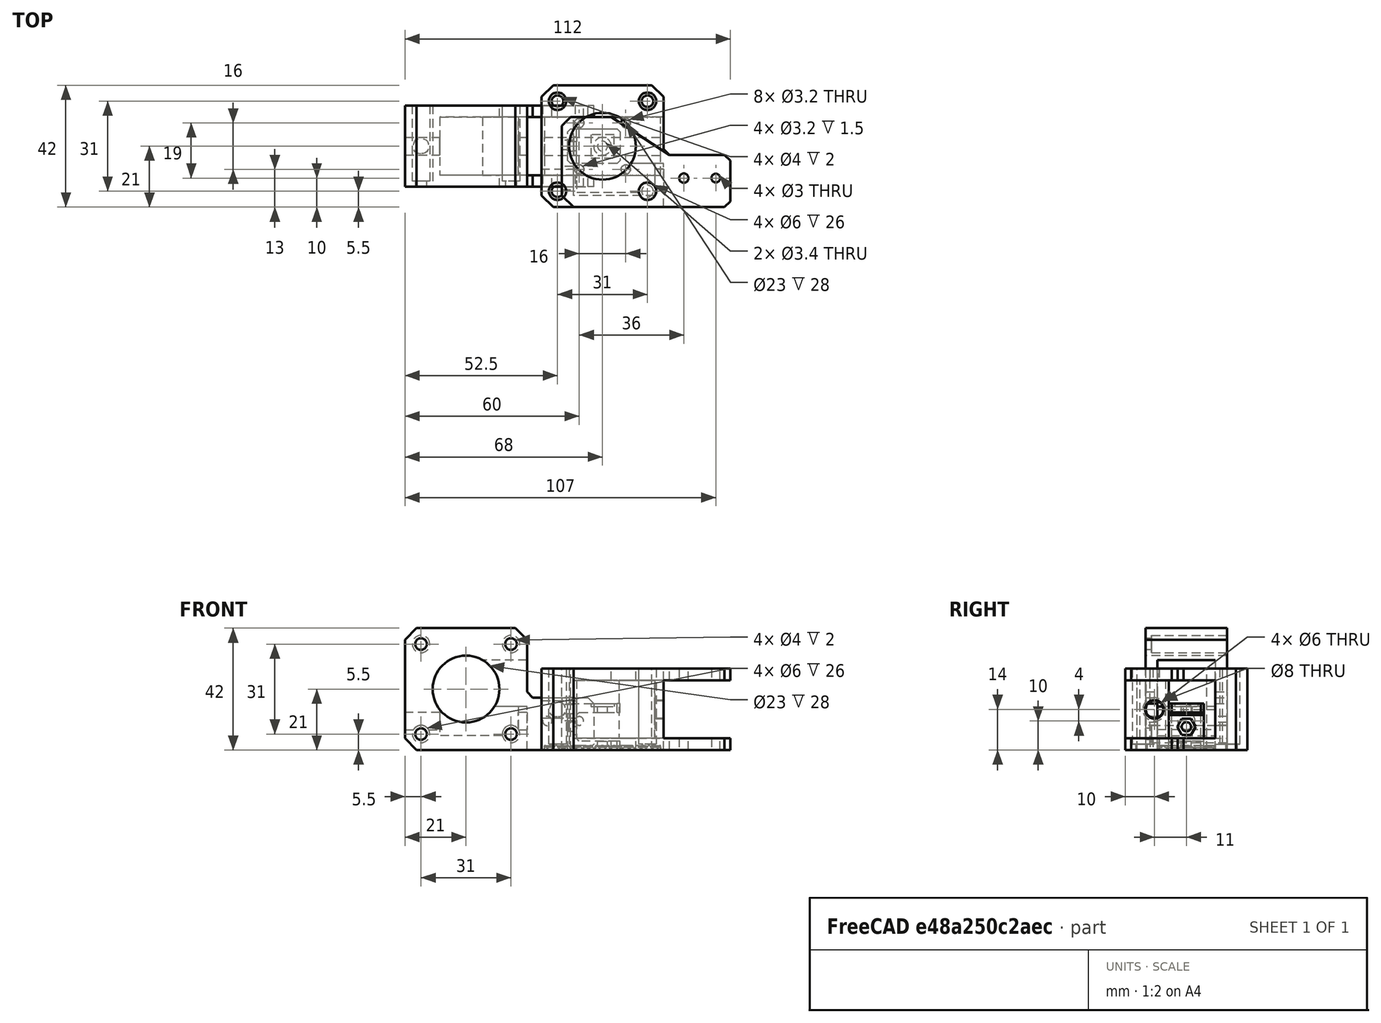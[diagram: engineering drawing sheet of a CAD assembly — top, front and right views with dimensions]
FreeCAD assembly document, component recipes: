
FREECAD ASSEMBLY — COMPONENT RECIPES ("LinearRailMod")

This assembly document has 5 components, labeled P0..P4 below (a component is one placed body or linked part). 5 of them carry a construction recipe — the FreeCAD feature program that regenerates the part from scratch, quoted from this document or its linked companion documents; the rest are supplied as boundary geometry only. No exploded tour is included for this assembly.
COMPONENT P0 — recipe-attached ("Motor", modeled in this document).
Construction recipe (the document's own serialized feature program — sketch geometry with constraints, then the solid features built on it; lengths are millimeters unless a unit is written):

FEATURE [Sketcher::SketchObject] Sketch
  ArcFitTolerance = 1e-06
  AttachmentSupport = -> [XY_Plane001]
  FullyConstrained = false
  MakeInternals = false
  MapMode = 5
  sketch-geometry (20):
    g0: GeomPoint [constr] X=0 Y=0 Z=0
    g1: LineSegment StartX=-17 StartY=21 StartZ=0 EndX=-21 EndY=17 EndZ=0
    g2: LineSegment StartX=-21 StartY=-17 StartZ=0 EndX=-17 EndY=-21 EndZ=0
    g3: LineSegment StartX=17 StartY=21 StartZ=0 EndX=21 EndY=17 EndZ=0
    g4: Circle CenterX=-15.5 CenterY=-15.5 CenterZ=0 NormalX=0 NormalY=0 NormalZ=1 AngleXU=0 Radius=2
    g5: Circle CenterX=15.5 CenterY=-15.5 CenterZ=0 NormalX=0 NormalY=0 NormalZ=1 AngleXU=0 Radius=2
    g6: Circle CenterX=15.5 CenterY=15.5 CenterZ=0 NormalX=0 NormalY=0 NormalZ=1 AngleXU=0 Radius=2
    g7: LineSegment StartX=-21 StartY=17 StartZ=0 EndX=-21 EndY=-17 EndZ=0
    g8: LineSegment StartX=-17 StartY=-21 StartZ=0 EndX=42 EndY=-21 EndZ=0
    g9: LineSegment StartX=-17 StartY=21 StartZ=0 EndX=17 EndY=21 EndZ=0
    g10: LineSegment StartX=21 StartY=17 StartZ=0 EndX=21 EndY=-1 EndZ=0
    g11: LineSegment StartX=44 StartY=-19 StartZ=0 EndX=42 EndY=-21 EndZ=0
    g12: Circle CenterX=-15.5 CenterY=15.5 CenterZ=0 NormalX=0 NormalY=0 NormalZ=1 AngleXU=0 Radius=2
    g13: Circle CenterX=0 CenterY=0 CenterZ=0 NormalX=0 NormalY=0 NormalZ=1 AngleXU=0 Radius=11.5
    g14: Circle CenterX=28 CenterY=-11 CenterZ=0 NormalX=0 NormalY=0 NormalZ=1 AngleXU=0 Radius=1.6
    g15: LineSegment StartX=21 StartY=-1 StartZ=0 EndX=23 EndY=-3 EndZ=0
    g16: LineSegment StartX=23 StartY=-3 StartZ=0 EndX=42 EndY=-3 EndZ=0
    g17: LineSegment StartX=42 StartY=-3 StartZ=0 EndX=44 EndY=-5 EndZ=0
    g18: LineSegment StartX=44 StartY=-5 StartZ=0 EndX=44 EndY=-19 EndZ=0
    g19: Circle CenterX=39 CenterY=-11 CenterZ=0 NormalX=0 NormalY=0 NormalZ=1 AngleXU=0 Radius=1.5
  constraints (19):
    c: Coincident(g7,g1)
    c: Coincident(g7,g2)
    c: Vertical(g7)
    c: Coincident(g8,g2)
    c: Horizontal(g8)
    c: Coincident(g9,g1)
    c: Coincident(g9,g3)
    c: Horizontal(g9)
    c: Coincident(g10,g3)
    c: Vertical(g10)
    c: Coincident(g11,g8)
    c: Coincident(g13,g0)
    c: Coincident(g15,g10)
    c: Coincident(g16,g15)
    c: Horizontal(g16)
    c: Coincident(g17,g16)
    c: Coincident(g18,g17)
    c: Coincident(g18,g11)
    c: Vertical(g18)
FEATURE [PartDesign::Pad] Pad
  Direction = (0,0,1)
  Length = 28
  Length2 = 10
  Profile = -> Sketch
  ReferenceAxis = -> Sketch [N_Axis]
  Refine = true
  Suppressed = false
  Type = 0
FEATURE [Sketcher::SketchObject] Sketch003
  ArcFitTolerance = 1e-06
  AttachmentSupport = -> [Pad]
  FullyConstrained = false
  MakeInternals = false
  MapMode = 5
  Placement = pos=(0,-21,0) rot=(1,0,0;1.5708rad)
  sketch-geometry (4):
    g0: LineSegment StartX=21 StartY=24 StartZ=0 EndX=21 EndY=4 EndZ=0
    g1: LineSegment StartX=21 StartY=4 StartZ=0 EndX=50 EndY=4 EndZ=0
    g2: LineSegment StartX=50 StartY=4 StartZ=0 EndX=50 EndY=24 EndZ=0
    g3: LineSegment StartX=50 StartY=24 StartZ=0 EndX=21 EndY=24 EndZ=0
  constraints (8):
    c: Coincident(g0,g1)
    c: Coincident(g1,g2)
    c: Coincident(g2,g3)
    c: Coincident(g3,g0)
    c: Vertical(g0)
    c: Vertical(g2)
    c: Horizontal(g1)
    c: Horizontal(g3)
FEATURE [PartDesign::Pocket] Pocket
  BaseFeature = -> Pad
  Direction = (0,1,-2e-16)
  Length = 42
  Length2 = 5
  Profile = -> Sketch003
  ReferenceAxis = -> Sketch003 [N_Axis]
  Refine = true
  Suppressed = false
  Type = 0
FEATURE [Sketcher::SketchObject] Sketch004
  ArcFitTolerance = 1e-06
  AttachmentSupport = -> [Pocket]
  FullyConstrained = false
  MakeInternals = false
  MapMode = 5
  Placement = pos=(0,0,28) rot=(0,0,1;0rad)
  sketch-geometry (4):
    g0: Circle CenterX=-15.5 CenterY=-15.5 CenterZ=0 NormalX=0 NormalY=0 NormalZ=1 AngleXU=0 Radius=3
    g1: Circle CenterX=-15.5 CenterY=15.5 CenterZ=0 NormalX=0 NormalY=0 NormalZ=1 AngleXU=0 Radius=3
    g2: Circle CenterX=15.5 CenterY=15.5 CenterZ=0 NormalX=0 NormalY=0 NormalZ=1 AngleXU=0 Radius=3
    g3: Circle CenterX=15.5 CenterY=-15.5 CenterZ=0 NormalX=0 NormalY=0 NormalZ=1 AngleXU=0 Radius=3
FEATURE [PartDesign::Pocket] Pocket001
  BaseFeature = -> Pocket
  Direction = (0,0,-1)
  Length = 26
  Length2 = 5
  Profile = -> Sketch004
  ReferenceAxis = -> Sketch004 [N_Axis]
  Refine = true
  Suppressed = false
  Type = 0
FEATURE [Sketcher::SketchObject] Sketch005
  ArcFitTolerance = 1e-06
  AttachmentSupport = -> [Pocket001]
  FullyConstrained = false
  MakeInternals = false
  MapMode = 5
  Placement = pos=(21,0,0) rot=(0.57735,0.57735,0.57735;2.0944rad)
  sketch-geometry (1):
    g0: Circle CenterX=-11 CenterY=14 CenterZ=0 NormalX=0 NormalY=0 NormalZ=1 AngleXU=0 Radius=3
FEATURE [PartDesign::Pocket] Pocket002
  BaseFeature = -> Pocket001
  Direction = (-1,0,0)
  Length = 42
  Length2 = 5
  Profile = -> Sketch005
  ReferenceAxis = -> Sketch005 [N_Axis]
  Refine = true
  Suppressed = false
  Type = 0
FEATURE [Sketcher::SketchObject] Sketch006
  ArcFitTolerance = 1e-06
  AttachmentSupport = -> [Pocket002]
  FullyConstrained = false
  MakeInternals = false
  MapMode = 5
  Placement = pos=(21,0,0) rot=(0.57735,0.57735,0.57735;2.0944rad)
  sketch-geometry (4):
    g0: LineSegment StartX=-6 StartY=24 StartZ=0 EndX=-6 EndY=4 EndZ=0
    g1: LineSegment StartX=-6 StartY=4 StartZ=0 EndX=10 EndY=4 EndZ=0
    g2: LineSegment StartX=10 StartY=4 StartZ=0 EndX=10 EndY=24 EndZ=0
    g3: LineSegment StartX=10 StartY=24 StartZ=0 EndX=-6 EndY=24 EndZ=0
  constraints (8):
    c: Coincident(g0,g1)
    c: Coincident(g1,g2)
    c: Coincident(g2,g3)
    c: Coincident(g3,g0)
    c: Vertical(g0)
    c: Vertical(g2)
    c: Horizontal(g1)
    c: Horizontal(g3)
FEATURE [PartDesign::Pocket] Pocket003
  BaseFeature = -> Pocket002
  Direction = (-1,0,0)
  Length = 16
  Length2 = 5
  Profile = -> Sketch006
  ReferenceAxis = -> Sketch006 [N_Axis]
  Refine = true
  Suppressed = false
  Type = 0
FEATURE [Sketcher::SketchObject] Sketch007
  ArcFitTolerance = 1e-06
  AttachmentSupport = -> [Pocket003]
  FullyConstrained = false
  MakeInternals = false
  MapMode = 5
  Placement = pos=(0,-6,0) rot=(0,0.707107,0.707107;3.14159rad)
  sketch-geometry (4):
    g0: LineSegment StartX=-18 StartY=24.038 StartZ=0 EndX=-18 EndY=4.03804 EndZ=0
    g1: LineSegment StartX=-18 StartY=4.03804 StartZ=0 EndX=9 EndY=4.03804 EndZ=0
    g2: LineSegment StartX=9 StartY=4.03804 StartZ=0 EndX=9 EndY=24.038 EndZ=0
    g3: LineSegment StartX=9 StartY=24.038 StartZ=0 EndX=-18 EndY=24.038 EndZ=0
  constraints (8):
    c: Coincident(g0,g1)
    c: Coincident(g1,g2)
    c: Coincident(g2,g3)
    c: Coincident(g3,g0)
    c: Vertical(g0)
    c: Vertical(g2)
    c: Horizontal(g1)
    c: Horizontal(g3)
FEATURE [PartDesign::Pocket] Pocket004
  BaseFeature = -> Pocket003
  Direction = (0,-1,2e-16)
  Length = 10
  Length2 = 5
  Profile = -> Sketch007
  ReferenceAxis = -> Sketch007 [N_Axis]
  Refine = true
  Suppressed = false
  Type = 0
FEATURE [PartDesign::Body] Body
  AllowCompound = false
  Group = -> [Sketch,Pad,Sketch003,Pocket,Sketch004,Pocket001,Sketch005,Pocket002,Sketch006,Pocket003,Sketch007,Pocket004]
  Origin = -> Origin001
  Tip = -> Pocket004
COMPONENT P1 — recipe-attached ("IdlerGearFrame", modeled in this document).
Construction recipe (the document's own serialized feature program — sketch geometry with constraints, then the solid features built on it; lengths are millimeters unless a unit is written):

FEATURE [Sketcher::SketchObject] Sketch008
  ArcFitTolerance = 1e-06
  AttachmentSupport = -> [XY_Plane007]
  FullyConstrained = false
  MakeInternals = false
  MapMode = 5
  sketch-geometry (12):
    g0: LineSegment StartX=-14 StartY=-17 StartZ=0 EndX=-10 EndY=-21 EndZ=0
    g1: LineSegment StartX=-14 StartY=7 StartZ=0 EndX=-14 EndY=-17 EndZ=0
    g2: LineSegment StartX=-10 StartY=-21 StartZ=0 EndX=42 EndY=-21 EndZ=0
    g3: LineSegment StartX=44 StartY=-19 StartZ=0 EndX=42 EndY=-21 EndZ=0
    g4: Circle CenterX=28 CenterY=-11 CenterZ=0 NormalX=0 NormalY=0 NormalZ=1 AngleXU=0 Radius=1.6
    g5: LineSegment StartX=23 StartY=-3 StartZ=0 EndX=42 EndY=-3 EndZ=0
    g6: LineSegment StartX=42 StartY=-3 StartZ=0 EndX=44 EndY=-5 EndZ=0
    g7: LineSegment StartX=44 StartY=-5 StartZ=0 EndX=44 EndY=-19 EndZ=0
    g8: Circle CenterX=39 CenterY=-11 CenterZ=0 NormalX=0 NormalY=0 NormalZ=1 AngleXU=0 Radius=1.5
    g9: LineSegment StartX=23 StartY=-3 StartZ=0 EndX=3 EndY=10 EndZ=0
    g10: LineSegment StartX=3 StartY=10 StartZ=0 EndX=-11 EndY=10 EndZ=0
    g11: LineSegment StartX=-11 StartY=10 StartZ=0 EndX=-14 EndY=7 EndZ=0
  constraints (15):
    c: Coincident(g1,g0)
    c: Vertical(g1)
    c: Coincident(g2,g0)
    c: Horizontal(g2)
    c: Coincident(g3,g2)
    c: Horizontal(g5)
    c: Coincident(g6,g5)
    c: Coincident(g7,g6)
    c: Coincident(g7,g3)
    c: Vertical(g7)
    c: Coincident(g5,g9)
    c: Coincident(g9,g10)
    c: Horizontal(g10)
    c: Coincident(g10,g11)
    c: Coincident(g11,g1)
FEATURE [PartDesign::Pad] Pad002
  Direction = (0,0,1)
  Length = 28
  Length2 = 10
  Profile = -> Sketch008
  ReferenceAxis = -> Sketch008 [N_Axis]
  Refine = true
  Suppressed = false
  Type = 0
FEATURE [Sketcher::SketchObject] Sketch018
  ArcFitTolerance = 1e-06
  AttachmentSupport = -> [Pad002]
  FullyConstrained = false
  MakeInternals = false
  MapMode = 5
  Placement = pos=(0,-21,0) rot=(1,0,0;1.5708rad)
  sketch-geometry (4):
    g0: LineSegment StartX=21 StartY=24 StartZ=0 EndX=21 EndY=4 EndZ=0
    g1: LineSegment StartX=21 StartY=4 StartZ=0 EndX=50 EndY=4 EndZ=0
    g2: LineSegment StartX=50 StartY=4 StartZ=0 EndX=50 EndY=24 EndZ=0
    g3: LineSegment StartX=50 StartY=24 StartZ=0 EndX=21 EndY=24 EndZ=0
  constraints (8):
    c: Coincident(g0,g1)
    c: Coincident(g1,g2)
    c: Coincident(g2,g3)
    c: Coincident(g3,g0)
    c: Vertical(g0)
    c: Vertical(g2)
    c: Horizontal(g1)
    c: Horizontal(g3)
FEATURE [PartDesign::Pocket] Pocket011
  BaseFeature = -> Pad002
  Direction = (0,1,-2e-16)
  Length = 42
  Length2 = 5
  Profile = -> Sketch018
  ReferenceAxis = -> Sketch018 [N_Axis]
  Refine = true
  Suppressed = false
  Type = 0
FEATURE [Sketcher::SketchObject] Sketch020
  ArcFitTolerance = 1e-06
  FullyConstrained = false
  MakeInternals = false
  MapMode = 5
  Placement = pos=(21,0,0) rot=(0.57735,0.57735,0.57735;2.0944rad)
  sketch-geometry (4):
    g0: LineSegment StartX=-6 StartY=24 StartZ=0 EndX=-6 EndY=4 EndZ=0
    g1: LineSegment StartX=-6 StartY=4 StartZ=0 EndX=17 EndY=4 EndZ=0
    g2: LineSegment StartX=17 StartY=4 StartZ=0 EndX=17 EndY=24 EndZ=0
    g3: LineSegment StartX=17 StartY=24 StartZ=0 EndX=-6 EndY=24 EndZ=0
  constraints (8):
    c: Coincident(g0,g1)
    c: Coincident(g1,g2)
    c: Coincident(g2,g3)
    c: Coincident(g3,g0)
    c: Vertical(g0)
    c: Vertical(g2)
    c: Horizontal(g1)
    c: Horizontal(g3)
FEATURE [PartDesign::Pocket] Pocket013
  BaseFeature = -> Pocket011
  Direction = (-1,0,0)
  Length = 31
  Length2 = 5
  Profile = -> Sketch020
  ReferenceAxis = -> Sketch020 [N_Axis]
  Refine = true
  Suppressed = false
  Type = 0
FEATURE [Sketcher::SketchObject] Sketch021
  ArcFitTolerance = 1e-06
  AttachmentSupport = -> [Pocket013]
  FullyConstrained = false
  MakeInternals = false
  MapMode = 5
  Placement = pos=(0,-6,0) rot=(0,0.707107,0.707107;3.14159rad)
  sketch-geometry (4):
    g0: LineSegment StartX=10 StartY=24 StartZ=0 EndX=-18 EndY=24 EndZ=0
    g1: LineSegment StartX=-18 StartY=24 StartZ=0 EndX=-18 EndY=4 EndZ=0
    g2: LineSegment StartX=-18 StartY=4 StartZ=0 EndX=10 EndY=4 EndZ=0
    g3: LineSegment StartX=10 StartY=4 StartZ=0 EndX=10 EndY=24 EndZ=0
  constraints (8):
    c: Coincident(g0,g1)
    c: Coincident(g1,g2)
    c: Coincident(g2,g3)
    c: Coincident(g3,g0)
    c: Horizontal(g0)
    c: Horizontal(g2)
    c: Vertical(g1)
    c: Vertical(g3)
FEATURE [PartDesign::Pocket] Pocket014
  BaseFeature = -> Pocket013
  Direction = (0,-1,2e-16)
  Length = 11
  Length2 = 5
  Profile = -> Sketch021
  ReferenceAxis = -> Sketch021 [N_Axis]
  Refine = true
  Suppressed = false
  Type = 0
FEATURE [Sketcher::SketchObject] Sketch022
  ArcFitTolerance = 1e-06
  AttachmentSupport = -> [Pocket014]
  FullyConstrained = false
  MakeInternals = false
  MapMode = 5
  Placement = pos=(21,0,0) rot=(0.57735,0.57735,0.57735;2.0944rad)
  sketch-geometry (1):
    g0: Circle CenterX=-11 CenterY=14 CenterZ=0 NormalX=0 NormalY=0 NormalZ=1 AngleXU=0 Radius=3.2
FEATURE [PartDesign::Pocket] Pocket015
  BaseFeature = -> Pocket014
  Direction = (-1,0,0)
  Length = 5
  Length2 = 5
  Profile = -> Sketch022
  ReferenceAxis = -> Sketch022 [N_Axis]
  Refine = true
  Suppressed = false
  Type = 0
FEATURE [Sketcher::SketchObject] Sketch023
  ArcFitTolerance = 1e-06
  AttachmentSupport = -> [Pocket015]
  FullyConstrained = false
  MakeInternals = false
  MapMode = 5
  Placement = pos=(-14,0,0) rot=(0.57735,-0.57735,-0.57735;2.0944rad)
  sketch-geometry (2):
    g0: Circle CenterX=11 CenterY=14 CenterZ=0 NormalX=0 NormalY=0 NormalZ=1 AngleXU=0 Radius=4
    g1: Circle CenterX=-0.5 CenterY=14 CenterZ=0 NormalX=0 NormalY=0 NormalZ=1 AngleXU=0 Radius=1.6
FEATURE [PartDesign::Pocket] Pocket016
  BaseFeature = -> Pocket015
  Direction = (1,0,0)
  Length = 5
  Length2 = 5
  Profile = -> Sketch023
  ReferenceAxis = -> Sketch023 [N_Axis]
  Refine = true
  Suppressed = false
  Type = 0
FEATURE [PartDesign::Body] Body002
  AllowCompound = false
  Group = -> [Sketch008,Pad002,Sketch018,Pocket011,Sketch020,Pocket013,Sketch021,Pocket014,Sketch022,Pocket015,Sketch023,Pocket016]
  Origin = -> Origin007
  Tip = -> Pocket016
COMPONENT P2 — recipe-attached ("IdlerGear", modeled in this document).
Construction recipe (the document's own serialized feature program — sketch geometry with constraints, then the solid features built on it; lengths are millimeters unless a unit is written):

FEATURE [Sketcher::SketchObject] Sketch009
  ArcFitTolerance = 1e-06
  AttachmentSupport = -> [XY_Plane006]
  FullyConstrained = false
  MakeInternals = false
  MapMode = 5
  sketch-geometry (10):
    g0: Circle [constr] CenterX=0 CenterY=0 CenterZ=0 NormalX=0 NormalY=0 NormalZ=1 AngleXU=0 Radius=6.5
    g1: LineSegment StartX=-12 StartY=5 StartZ=0 EndX=-11 EndY=6 EndZ=0
    g2: LineSegment StartX=-11 StartY=6 StartZ=0 EndX=5 EndY=6 EndZ=0
    g3: LineSegment StartX=5 StartY=6 StartZ=0 EndX=6 EndY=5 EndZ=0
    g4: LineSegment StartX=6 StartY=5 StartZ=0 EndX=6 EndY=-5 EndZ=0
    g5: LineSegment StartX=6 StartY=-5 StartZ=0 EndX=5 EndY=-6 EndZ=0
    g6: LineSegment StartX=5 StartY=-6 StartZ=0 EndX=-11 EndY=-6 EndZ=0
    g7: LineSegment StartX=-11 StartY=-6 StartZ=0 EndX=-12 EndY=-5 EndZ=0
    g8: LineSegment StartX=-12 StartY=-5 StartZ=0 EndX=-12 EndY=5 EndZ=0
    g9: Circle CenterX=0 CenterY=0 CenterZ=0 NormalX=0 NormalY=0 NormalZ=1 AngleXU=0 Radius=1.6
  constraints (12):
    c: Coincident(g1,g2)
    c: Horizontal(g2)
    c: Coincident(g2,g3)
    c: Coincident(g3,g4)
    c: Vertical(g4)
    c: Coincident(g4,g5)
    c: Coincident(g5,g6)
    c: Horizontal(g6)
    c: Coincident(g6,g7)
    c: Coincident(g7,g8)
    c: Coincident(g8,g1)
    c: Vertical(g8)
FEATURE [PartDesign::Pad] Pad001
  Direction = (0,0,1)
  Length = 16
  Length2 = 10
  Profile = -> Sketch009
  ReferenceAxis = -> Sketch009 [N_Axis]
  Refine = true
  Suppressed = false
  Type = 0
FEATURE [Sketcher::SketchObject] Sketch013
  ArcFitTolerance = 1e-06
  FullyConstrained = false
  MakeInternals = false
  MapMode = 5
  Placement = pos=(0,-6,0) rot=(1,0,0;1.5708rad)
  sketch-geometry (6):
    g0: LineSegment StartX=-9 StartY=12 StartZ=0 EndX=-8 EndY=13 EndZ=0
    g1: LineSegment StartX=-8 StartY=13 StartZ=0 EndX=5 EndY=13 EndZ=0
    g2: LineSegment StartX=5 StartY=13 StartZ=0 EndX=5 EndY=3 EndZ=0
    g3: LineSegment StartX=5 StartY=3 StartZ=0 EndX=-8 EndY=3 EndZ=0
    g4: LineSegment StartX=-8 StartY=3 StartZ=0 EndX=-9 EndY=4 EndZ=0
    g5: LineSegment StartX=-9 StartY=4 StartZ=0 EndX=-9 EndY=12 EndZ=0
  constraints (10):
    c: Coincident(g0,g1)
    c: Horizontal(g1)
    c: Coincident(g1,g2)
    c: Vertical(g2)
    c: Coincident(g2,g3)
    c: Horizontal(g3)
    c: Coincident(g3,g4)
    c: Coincident(g4,g5)
    c: Coincident(g5,g0)
    c: Vertical(g5)
FEATURE [Sketcher::SketchObject] Sketch014
  ArcFitTolerance = 1e-06
  FullyConstrained = false
  MakeInternals = false
  MapMode = 5
  Placement = pos=(5,0,0) rot=(0.57735,-0.57735,-0.57735;2.0944rad)
  sketch-geometry (4):
    g0: LineSegment StartX=-6 StartY=13 StartZ=0 EndX=-6 EndY=3 EndZ=0
    g1: LineSegment StartX=-6 StartY=3 StartZ=0 EndX=6 EndY=3 EndZ=0
    g2: LineSegment StartX=6 StartY=3 StartZ=0 EndX=6 EndY=13 EndZ=0
    g3: LineSegment StartX=6 StartY=13 StartZ=0 EndX=-6 EndY=13 EndZ=0
  constraints (8):
    c: Coincident(g0,g1)
    c: Coincident(g1,g2)
    c: Coincident(g2,g3)
    c: Coincident(g3,g0)
    c: Vertical(g0)
    c: Vertical(g2)
    c: Horizontal(g1)
    c: Horizontal(g3)
FEATURE [PartDesign::Pocket] Pocket006
  BaseFeature = -> Pad001
  Direction = (0,1,-2e-16)
  Length = 12
  Length2 = 5
  Profile = -> Sketch013
  ReferenceAxis = -> Sketch013 [N_Axis]
  Refine = true
  Suppressed = false
  Type = 0
FEATURE [PartDesign::Pocket] Pocket007
  BaseFeature = -> Pocket006
  Direction = (1,-1e-16,1e-16)
  Length = 1
  Length2 = 5
  Profile = -> Sketch014
  ReferenceAxis = -> Sketch014 [N_Axis]
  Refine = true
  Suppressed = false
  Type = 0
FEATURE [Sketcher::SketchObject] Sketch015
  ArcFitTolerance = 1e-06
  AttachmentSupport = -> [Pocket007]
  FullyConstrained = false
  MakeInternals = false
  MapMode = 5
  Placement = pos=(-12,0,0) rot=(0.57735,-0.57735,-0.57735;2.0944rad)
  sketch-geometry (1):
    g0: Circle CenterX=0 CenterY=8 CenterZ=0 NormalX=0 NormalY=0 NormalZ=1 AngleXU=0 Radius=1.6
FEATURE [PartDesign::Pocket] Pocket008
  BaseFeature = -> Pocket007
  Direction = (1,0,0)
  Length = 3
  Length2 = 5
  Profile = -> Sketch015
  ReferenceAxis = -> Sketch015 [N_Axis]
  Refine = true
  Suppressed = false
  Type = 0
FEATURE [Sketcher::SketchObject] Sketch016
  ArcFitTolerance = 1e-06
  AttachmentSupport = -> [Pocket008]
  FullyConstrained = false
  MakeInternals = false
  MapMode = 5
  Placement = pos=(0,0,16) rot=(0,0,1;0rad)
  sketch-geometry (5):
    g0: LineSegment StartX=-4 StartY=-4 StartZ=0 EndX=4 EndY=-4 EndZ=0
    g1: LineSegment StartX=4 StartY=-4 StartZ=0 EndX=4 EndY=4 EndZ=0
    g2: LineSegment StartX=4 StartY=4 StartZ=0 EndX=-4 EndY=4 EndZ=0
    g3: LineSegment StartX=-4 StartY=4 StartZ=0 EndX=-4 EndY=-4 EndZ=0
    g4: GeomPoint [constr] X=0 Y=0 Z=0
  constraints (10):
    c: Coincident(g0,g1)
    c: Coincident(g1,g2)
    c: Coincident(g2,g3)
    c: Coincident(g3,g0)
    c: Horizontal(g0)
    c: Horizontal(g2)
    c: Vertical(g1)
    c: Vertical(g3)
    c: Symmetric(g2,g0,g4)
    c: Coincident(g4,g-1)
FEATURE [PartDesign::Pocket] Pocket009
  BaseFeature = -> Pocket008
  Direction = (0,0,-1)
  Length = 1
  Length2 = 5
  Profile = -> Sketch016
  ReferenceAxis = -> Sketch016 [N_Axis]
  Refine = true
  Suppressed = false
  Type = 0
FEATURE [Sketcher::SketchObject] Sketch017
  ArcFitTolerance = 1e-06
  AttachmentSupport = -> [Pocket009]
  FullyConstrained = false
  MakeInternals = false
  MapMode = 5
  Placement = pos=(-9,0,0) rot=(0.57735,0.57735,0.57735;2.0944rad)
  sketch-geometry (7):
    g0: LineSegment StartX=3.2 StartY=8 StartZ=0 EndX=1.6 EndY=10.7713 EndZ=0
    g1: LineSegment StartX=1.6 StartY=10.7713 StartZ=0 EndX=-1.6 EndY=10.7713 EndZ=0
    g2: LineSegment StartX=-1.6 StartY=10.7713 StartZ=0 EndX=-3.2 EndY=8 EndZ=0
    g3: LineSegment StartX=-3.2 StartY=8 StartZ=0 EndX=-1.6 EndY=5.22872 EndZ=0
    g4: LineSegment StartX=-1.6 StartY=5.22872 StartZ=0 EndX=1.6 EndY=5.22872 EndZ=0
    g5: LineSegment StartX=1.6 StartY=5.22872 StartZ=0 EndX=3.2 EndY=8 EndZ=0
    g6: Circle [constr] CenterX=0 CenterY=8 CenterZ=0 NormalX=0 NormalY=0 NormalZ=1 AngleXU=0 Radius=3.2
  constraints (13):
    c: Coincident(g0,g1)
    c: Coincident(g1,g2)
    c: Coincident(g2,g3)
    c: Coincident(g3,g4)
    c: Coincident(g4,g5)
    c: Coincident(g5,g0)
    c: Equal(g0, g1-g5) x5
    c: PointOnObject(g0,g6)
    c: PointOnObject(g1,g6)
    c: PointOnObject(g2,g6)
    c: PointOnObject(g3,g6)
    c: PointOnObject(g4,g6)
    c: PointOnObject(g5,g6)
FEATURE [PartDesign::Pocket] Pocket010
  BaseFeature = -> Pocket009
  Direction = (-1,0,0)
  Length = 1
  Length2 = 5
  Profile = -> Sketch017
  ReferenceAxis = -> Sketch017 [N_Axis]
  Refine = true
  Suppressed = false
  Type = 0
FEATURE [PartDesign::Hole] Hole
  BaseFeature = -> Pocket010
  CustomThreadClearance = 0
  Depth = 25
  DepthType = 0
  Diameter = 3.4
  DrillForDepth = false
  DrillPoint = 1
  DrillPointAngle = 118
  HoleCutCountersinkAngle = 90
  HoleCutCustomValues = false
  HoleCutDepth = 0
  HoleCutDiameter = 6.1
  HoleCutType = 2
  ModelThread = false
  Profile = -> Pocket010 [Face4]
  Refine = true
  Suppressed = false
  Tapered = false
  TaperedAngle = 90
  ThreadClass = 0
  ThreadDepth = 25
  ThreadDepthType = 0
  ThreadDirection = 0
  ThreadFit = 0
  ThreadSize = 9
  ThreadType = 1
  Threaded = false
  UseCustomThreadClearance = false
FEATURE [PartDesign::Body] Body001
  AllowCompound = false
  Group = -> [Sketch009,Pad001,Sketch013,Sketch014,Pocket006,Pocket007,Sketch015,Pocket008,Sketch016,Pocket009,Sketch017,Pocket010,Hole]
  Origin = -> Origin006
  Tip = -> Hole
COMPONENT P3 — recipe-attached ("Base", modeled in this document).
Construction recipe (the document's own serialized feature program — sketch geometry with constraints, then the solid features built on it; lengths are millimeters unless a unit is written):

FEATURE [Sketcher::SketchObject] Sketch024
  ArcFitTolerance = 1e-06
  AttachmentSupport = -> [XY_Plane010]
  FullyConstrained = false
  MakeInternals = false
  MapMode = 5
  sketch-geometry (5):
    g0: LineSegment StartX=-20 StartY=10 StartZ=0 EndX=-20 EndY=-10 EndZ=0
    g1: LineSegment StartX=-20 StartY=-10 StartZ=0 EndX=20 EndY=-10 EndZ=0
    g2: LineSegment StartX=20 StartY=-10 StartZ=0 EndX=20 EndY=10 EndZ=0
    g3: LineSegment StartX=20 StartY=10 StartZ=0 EndX=-20 EndY=10 EndZ=0
    g4: GeomPoint [constr] X=0 Y=0 Z=0
  constraints (9):
    c: Coincident(g0,g1)
    c: Coincident(g1,g2)
    c: Coincident(g2,g3)
    c: Coincident(g3,g0)
    c: Vertical(g0)
    c: Vertical(g2)
    c: Horizontal(g1)
    c: Horizontal(g3)
    c: Symmetric(g2,g0,g4)
FEATURE [PartDesign::Pad] Pad003
  Direction = (0,0,1)
  Length = 1.5
  Length2 = 10
  Profile = -> Sketch024
  ReferenceAxis = -> Sketch024 [N_Axis]
  Refine = true
  Suppressed = false
  Type = 0
FEATURE [Sketcher::SketchObject] Sketch025
  ArcFitTolerance = 1e-06
  AttachmentSupport = -> [Pad003]
  FullyConstrained = false
  MakeInternals = false
  MapMode = 5
  Placement = pos=(0,-10,0) rot=(1,0,0;1.5708rad)
  sketch-geometry (120):
    g0: ArcOfCircle CenterX=-19.7402 CenterY=1.35 CenterZ=0 NormalX=0 NormalY=0 NormalZ=1 AngleXU=0 Radius=0.149997 StartAngle=0.134719 EndAngle=1.57082
    g1: ArcOfCircle CenterX=-18.2598 CenterY=1.35 CenterZ=0 NormalX=0 NormalY=0 NormalZ=1 AngleXU=0 Radius=0.15 StartAngle=1.5708 EndAngle=3.01411
    g2: ArcOfCircle CenterX=-19 CenterY=1.30511 CenterZ=0 NormalX=0 NormalY=0 NormalZ=1 AngleXU=0 Radius=0.555048 StartAngle=3.59519 EndAngle=5.83002
    g3: ArcOfCircle CenterX=-19.4 CenterY=1.5 CenterZ=0 NormalX=0 NormalY=0 NormalZ=1 AngleXU=0 Radius=1 StartAngle=5.82992 EndAngle=6.15188
    g4: ArcOfCircle CenterX=-18.6 CenterY=1.5 CenterZ=0 NormalX=0 NormalY=0 NormalZ=1 AngleXU=0 Radius=1 StartAngle=3.27181 EndAngle=3.5951
    g5: LineSegment StartX=-19.7402 StartY=1.5 StartZ=0 EndX=-18.2598 EndY=1.5 EndZ=0
    g6: ArcOfCircle CenterX=-17.7402 CenterY=1.35 CenterZ=0 NormalX=0 NormalY=0 NormalZ=1 AngleXU=0 Radius=0.149997 StartAngle=0.134719 EndAngle=1.57082
    g7: ArcOfCircle CenterX=-16.2598 CenterY=1.35 CenterZ=0 NormalX=0 NormalY=0 NormalZ=1 AngleXU=0 Radius=0.15 StartAngle=1.5708 EndAngle=3.01411
    g8: ArcOfCircle CenterX=-17 CenterY=1.30511 CenterZ=0 NormalX=0 NormalY=0 NormalZ=1 AngleXU=0 Radius=0.555048 StartAngle=3.59519 EndAngle=5.83002
    g9: ArcOfCircle CenterX=-17.4 CenterY=1.5 CenterZ=0 NormalX=0 NormalY=0 NormalZ=1 AngleXU=0 Radius=1 StartAngle=5.82992 EndAngle=6.15188
    g10: ArcOfCircle CenterX=-16.6 CenterY=1.5 CenterZ=0 NormalX=0 NormalY=0 NormalZ=1 AngleXU=0 Radius=1 StartAngle=3.27181 EndAngle=3.5951
    g11: LineSegment StartX=-17.7402 StartY=1.5 StartZ=0 EndX=-16.2598 EndY=1.5 EndZ=0
    g12: ArcOfCircle CenterX=-15.7402 CenterY=1.35 CenterZ=0 NormalX=0 NormalY=0 NormalZ=1 AngleXU=0 Radius=0.149997 StartAngle=0.134719 EndAngle=1.57082
    g13: ArcOfCircle CenterX=-14.2598 CenterY=1.35 CenterZ=0 NormalX=0 NormalY=0 NormalZ=1 AngleXU=0 Radius=0.15 StartAngle=1.5708 EndAngle=3.01411
    g14: ArcOfCircle CenterX=-15 CenterY=1.30511 CenterZ=0 NormalX=0 NormalY=0 NormalZ=1 AngleXU=0 Radius=0.555048 StartAngle=3.59519 EndAngle=5.83002
    g15: ArcOfCircle CenterX=-15.4 CenterY=1.5 CenterZ=0 NormalX=0 NormalY=0 NormalZ=1 AngleXU=0 Radius=1 StartAngle=5.82992 EndAngle=6.15188
    g16: ArcOfCircle CenterX=-14.6 CenterY=1.5 CenterZ=0 NormalX=0 NormalY=0 NormalZ=1 AngleXU=0 Radius=1 StartAngle=3.27181 EndAngle=3.5951
    g17: LineSegment StartX=-15.7402 StartY=1.5 StartZ=0 EndX=-14.2598 EndY=1.5 EndZ=0
    g18: ArcOfCircle CenterX=-13.7402 CenterY=1.35 CenterZ=0 NormalX=0 NormalY=0 NormalZ=1 AngleXU=0 Radius=0.149997 StartAngle=0.134719 EndAngle=1.57082
    g19: ArcOfCircle CenterX=-12.2598 CenterY=1.35 CenterZ=0 NormalX=0 NormalY=0 NormalZ=1 AngleXU=0 Radius=0.15 StartAngle=1.5708 EndAngle=3.01411
    g20: ArcOfCircle CenterX=-13 CenterY=1.30511 CenterZ=0 NormalX=0 NormalY=0 NormalZ=1 AngleXU=0 Radius=0.555048 StartAngle=3.59519 EndAngle=5.83002
    g21: ArcOfCircle CenterX=-13.4 CenterY=1.5 CenterZ=0 NormalX=0 NormalY=0 NormalZ=1 AngleXU=0 Radius=1 StartAngle=5.82992 EndAngle=6.15188
    g22: ArcOfCircle CenterX=-12.6 CenterY=1.5 CenterZ=0 NormalX=0 NormalY=0 NormalZ=1 AngleXU=0 Radius=1 StartAngle=3.27181 EndAngle=3.5951
    g23: LineSegment StartX=-13.7402 StartY=1.5 StartZ=0 EndX=-12.2598 EndY=1.5 EndZ=0
    g24: ArcOfCircle CenterX=-11.7402 CenterY=1.35 CenterZ=0 NormalX=0 NormalY=0 NormalZ=1 AngleXU=0 Radius=0.149997 StartAngle=0.134719 EndAngle=1.57082
    g25: ArcOfCircle CenterX=-10.2598 CenterY=1.35 CenterZ=0 NormalX=0 NormalY=0 NormalZ=1 AngleXU=0 Radius=0.15 StartAngle=1.5708 EndAngle=3.01411
    g26: ArcOfCircle CenterX=-11 CenterY=1.30511 CenterZ=0 NormalX=0 NormalY=0 NormalZ=1 AngleXU=0 Radius=0.555048 StartAngle=3.59519 EndAngle=5.83002
    g27: ArcOfCircle CenterX=-11.4 CenterY=1.5 CenterZ=0 NormalX=0 NormalY=0 NormalZ=1 AngleXU=0 Radius=1 StartAngle=5.82992 EndAngle=6.15188
    g28: ArcOfCircle CenterX=-10.6 CenterY=1.5 CenterZ=0 NormalX=0 NormalY=0 NormalZ=1 AngleXU=0 Radius=1 StartAngle=3.27181 EndAngle=3.5951
    g29: LineSegment StartX=-11.7402 StartY=1.5 StartZ=0 EndX=-10.2598 EndY=1.5 EndZ=0
    g30: ArcOfCircle CenterX=-9.74017 CenterY=1.35 CenterZ=0 NormalX=0 NormalY=0 NormalZ=1 AngleXU=0 Radius=0.149997 StartAngle=0.134719 EndAngle=1.57082
    g31: ArcOfCircle CenterX=-8.25982 CenterY=1.35 CenterZ=0 NormalX=0 NormalY=0 NormalZ=1 AngleXU=0 Radius=0.15 StartAngle=1.5708 EndAngle=3.01411
    g32: ArcOfCircle CenterX=-9 CenterY=1.30511 CenterZ=0 NormalX=0 NormalY=0 NormalZ=1 AngleXU=0 Radius=0.555048 StartAngle=3.59519 EndAngle=5.83002
    g33: ArcOfCircle CenterX=-9.4 CenterY=1.5 CenterZ=0 NormalX=0 NormalY=0 NormalZ=1 AngleXU=0 Radius=1 StartAngle=5.82992 EndAngle=6.15188
    g34: ArcOfCircle CenterX=-8.6 CenterY=1.5 CenterZ=0 NormalX=0 NormalY=0 NormalZ=1 AngleXU=0 Radius=1 StartAngle=3.27181 EndAngle=3.5951
    g35: LineSegment StartX=-9.74018 StartY=1.5 StartZ=0 EndX=-8.25982 EndY=1.5 EndZ=0
    g36: ArcOfCircle CenterX=-7.74017 CenterY=1.35 CenterZ=0 NormalX=0 NormalY=0 NormalZ=1 AngleXU=0 Radius=0.149997 StartAngle=0.134719 EndAngle=1.57082
    g37: ArcOfCircle CenterX=-6.25982 CenterY=1.35 CenterZ=0 NormalX=0 NormalY=0 NormalZ=1 AngleXU=0 Radius=0.15 StartAngle=1.5708 EndAngle=3.01411
    g38: ArcOfCircle CenterX=-7 CenterY=1.30511 CenterZ=0 NormalX=0 NormalY=0 NormalZ=1 AngleXU=0 Radius=0.555048 StartAngle=3.59519 EndAngle=5.83002
    g39: ArcOfCircle CenterX=-7.4 CenterY=1.5 CenterZ=0 NormalX=0 NormalY=0 NormalZ=1 AngleXU=0 Radius=1 StartAngle=5.82992 EndAngle=6.15188
    g40: ArcOfCircle CenterX=-6.6 CenterY=1.5 CenterZ=0 NormalX=0 NormalY=0 NormalZ=1 AngleXU=0 Radius=1 StartAngle=3.27181 EndAngle=3.5951
    g41: LineSegment StartX=-7.74018 StartY=1.5 StartZ=0 EndX=-6.25982 EndY=1.5 EndZ=0
    g42: ArcOfCircle CenterX=-5.74017 CenterY=1.35 CenterZ=0 NormalX=0 NormalY=0 NormalZ=1 AngleXU=0 Radius=0.149997 StartAngle=0.134719 EndAngle=1.57082
    g43: ArcOfCircle CenterX=-4.25982 CenterY=1.35 CenterZ=0 NormalX=0 NormalY=0 NormalZ=1 AngleXU=0 Radius=0.15 StartAngle=1.5708 EndAngle=3.01411
    g44: ArcOfCircle CenterX=-5 CenterY=1.30511 CenterZ=0 NormalX=0 NormalY=0 NormalZ=1 AngleXU=0 Radius=0.555048 StartAngle=3.59519 EndAngle=5.83002
    g45: ArcOfCircle CenterX=-5.4 CenterY=1.5 CenterZ=0 NormalX=0 NormalY=0 NormalZ=1 AngleXU=0 Radius=1 StartAngle=5.82992 EndAngle=6.15188
    g46: ArcOfCircle CenterX=-4.6 CenterY=1.5 CenterZ=0 NormalX=0 NormalY=0 NormalZ=1 AngleXU=0 Radius=1 StartAngle=3.27181 EndAngle=3.5951
    g47: LineSegment StartX=-5.74018 StartY=1.5 StartZ=0 EndX=-4.25982 EndY=1.5 EndZ=0
    g48: ArcOfCircle CenterX=-3.74017 CenterY=1.35 CenterZ=0 NormalX=0 NormalY=0 NormalZ=1 AngleXU=0 Radius=0.149997 StartAngle=0.134719 EndAngle=1.57082
    g49: ArcOfCircle CenterX=-2.25982 CenterY=1.35 CenterZ=0 NormalX=0 NormalY=0 NormalZ=1 AngleXU=0 Radius=0.15 StartAngle=1.5708 EndAngle=3.01411
    g50: ArcOfCircle CenterX=-3 CenterY=1.30511 CenterZ=0 NormalX=0 NormalY=0 NormalZ=1 AngleXU=0 Radius=0.555048 StartAngle=3.59519 EndAngle=5.83002
    g51: ArcOfCircle CenterX=-3.4 CenterY=1.5 CenterZ=0 NormalX=0 NormalY=0 NormalZ=1 AngleXU=0 Radius=1 StartAngle=5.82992 EndAngle=6.15188
    g52: ArcOfCircle CenterX=-2.6 CenterY=1.5 CenterZ=0 NormalX=0 NormalY=0 NormalZ=1 AngleXU=0 Radius=1 StartAngle=3.27181 EndAngle=3.5951
    g53: LineSegment StartX=-3.74018 StartY=1.5 StartZ=0 EndX=-2.25982 EndY=1.5 EndZ=0
    g54: ArcOfCircle CenterX=-1.74017 CenterY=1.35 CenterZ=0 NormalX=0 NormalY=0 NormalZ=1 AngleXU=0 Radius=0.149997 StartAngle=0.134719 EndAngle=1.57082
    g55: ArcOfCircle CenterX=-0.259824 CenterY=1.35 CenterZ=0 NormalX=0 NormalY=0 NormalZ=1 AngleXU=0 Radius=0.15 StartAngle=1.5708 EndAngle=3.01411
    g56: ArcOfCircle CenterX=-1 CenterY=1.30511 CenterZ=0 NormalX=0 NormalY=0 NormalZ=1 AngleXU=0 Radius=0.555048 StartAngle=3.59519 EndAngle=5.83002
    g57: ArcOfCircle CenterX=-1.4 CenterY=1.5 CenterZ=0 NormalX=0 NormalY=0 NormalZ=1 AngleXU=0 Radius=1 StartAngle=5.82992 EndAngle=6.15188
    g58: ArcOfCircle CenterX=-0.599999 CenterY=1.5 CenterZ=0 NormalX=0 NormalY=0 NormalZ=1 AngleXU=0 Radius=1 StartAngle=3.27181 EndAngle=3.5951
    g59: LineSegment StartX=-1.74018 StartY=1.5 StartZ=0 EndX=-0.259824 EndY=1.5 EndZ=0
    g60: ArcOfCircle CenterX=0.259827 CenterY=1.35 CenterZ=0 NormalX=0 NormalY=0 NormalZ=1 AngleXU=0 Radius=0.149997 StartAngle=0.134719 EndAngle=1.57082
    g61: ArcOfCircle CenterX=1.74018 CenterY=1.35 CenterZ=0 NormalX=0 NormalY=0 NormalZ=1 AngleXU=0 Radius=0.15 StartAngle=1.5708 EndAngle=3.01411
    g62: ArcOfCircle CenterX=1 CenterY=1.30511 CenterZ=0 NormalX=0 NormalY=0 NormalZ=1 AngleXU=0 Radius=0.555048 StartAngle=3.59519 EndAngle=5.83002
    g63: ArcOfCircle CenterX=0.599998 CenterY=1.5 CenterZ=0 NormalX=0 NormalY=0 NormalZ=1 AngleXU=0 Radius=1 StartAngle=5.82992 EndAngle=6.15188
    g64: ArcOfCircle CenterX=1.4 CenterY=1.5 CenterZ=0 NormalX=0 NormalY=0 NormalZ=1 AngleXU=0 Radius=1 StartAngle=3.27181 EndAngle=3.5951
    g65: LineSegment StartX=0.259824 StartY=1.5 StartZ=0 EndX=1.74018 EndY=1.5 EndZ=0
    g66: ArcOfCircle CenterX=2.25983 CenterY=1.35 CenterZ=0 NormalX=0 NormalY=0 NormalZ=1 AngleXU=0 Radius=0.149997 StartAngle=0.134719 EndAngle=1.57082
    g67: ArcOfCircle CenterX=3.74018 CenterY=1.35 CenterZ=0 NormalX=0 NormalY=0 NormalZ=1 AngleXU=0 Radius=0.15 StartAngle=1.5708 EndAngle=3.01411
    g68: ArcOfCircle CenterX=3 CenterY=1.30511 CenterZ=0 NormalX=0 NormalY=0 NormalZ=1 AngleXU=0 Radius=0.555048 StartAngle=3.59519 EndAngle=5.83002
    g69: ArcOfCircle CenterX=2.6 CenterY=1.5 CenterZ=0 NormalX=0 NormalY=0 NormalZ=1 AngleXU=0 Radius=1 StartAngle=5.82992 EndAngle=6.15188
    g70: ArcOfCircle CenterX=3.4 CenterY=1.5 CenterZ=0 NormalX=0 NormalY=0 NormalZ=1 AngleXU=0 Radius=1 StartAngle=3.27181 EndAngle=3.5951
    g71: LineSegment StartX=2.25982 StartY=1.5 StartZ=0 EndX=3.74018 EndY=1.5 EndZ=0
    g72: ArcOfCircle CenterX=4.25983 CenterY=1.35 CenterZ=0 NormalX=0 NormalY=0 NormalZ=1 AngleXU=0 Radius=0.149997 StartAngle=0.134719 EndAngle=1.57082
    g73: ArcOfCircle CenterX=5.74018 CenterY=1.35 CenterZ=0 NormalX=0 NormalY=0 NormalZ=1 AngleXU=0 Radius=0.15 StartAngle=1.5708 EndAngle=3.01411
    g74: ArcOfCircle CenterX=5 CenterY=1.30511 CenterZ=0 NormalX=0 NormalY=0 NormalZ=1 AngleXU=0 Radius=0.555048 StartAngle=3.59519 EndAngle=5.83002
    g75: ArcOfCircle CenterX=4.6 CenterY=1.5 CenterZ=0 NormalX=0 NormalY=0 NormalZ=1 AngleXU=0 Radius=1 StartAngle=5.82992 EndAngle=6.15188
    g76: ArcOfCircle CenterX=5.4 CenterY=1.5 CenterZ=0 NormalX=0 NormalY=0 NormalZ=1 AngleXU=0 Radius=1 StartAngle=3.27181 EndAngle=3.5951
    g77: LineSegment StartX=4.25982 StartY=1.5 StartZ=0 EndX=5.74018 EndY=1.5 EndZ=0
    g78: ArcOfCircle CenterX=6.25983 CenterY=1.35 CenterZ=0 NormalX=0 NormalY=0 NormalZ=1 AngleXU=0 Radius=0.149997 StartAngle=0.134719 EndAngle=1.57082
    g79: ArcOfCircle CenterX=7.74018 CenterY=1.35 CenterZ=0 NormalX=0 NormalY=0 NormalZ=1 AngleXU=0 Radius=0.15 StartAngle=1.5708 EndAngle=3.01411
    g80: ArcOfCircle CenterX=7 CenterY=1.30511 CenterZ=0 NormalX=0 NormalY=0 NormalZ=1 AngleXU=0 Radius=0.555048 StartAngle=3.59519 EndAngle=5.83002
    g81: ArcOfCircle CenterX=6.6 CenterY=1.5 CenterZ=0 NormalX=0 NormalY=0 NormalZ=1 AngleXU=0 Radius=1 StartAngle=5.82992 EndAngle=6.15188
    g82: ArcOfCircle CenterX=7.4 CenterY=1.5 CenterZ=0 NormalX=0 NormalY=0 NormalZ=1 AngleXU=0 Radius=1 StartAngle=3.27181 EndAngle=3.5951
    g83: LineSegment StartX=6.25982 StartY=1.5 StartZ=0 EndX=7.74018 EndY=1.5 EndZ=0
    g84: ArcOfCircle CenterX=8.25983 CenterY=1.35 CenterZ=0 NormalX=0 NormalY=0 NormalZ=1 AngleXU=0 Radius=0.149997 StartAngle=0.134719 EndAngle=1.57082
    g85: ArcOfCircle CenterX=9.74018 CenterY=1.35 CenterZ=0 NormalX=0 NormalY=0 NormalZ=1 AngleXU=0 Radius=0.15 StartAngle=1.5708 EndAngle=3.01411
    g86: ArcOfCircle CenterX=9 CenterY=1.30511 CenterZ=0 NormalX=0 NormalY=0 NormalZ=1 AngleXU=0 Radius=0.555048 StartAngle=3.59519 EndAngle=5.83002
    g87: ArcOfCircle CenterX=8.6 CenterY=1.5 CenterZ=0 NormalX=0 NormalY=0 NormalZ=1 AngleXU=0 Radius=1 StartAngle=5.82992 EndAngle=6.15188
    g88: ArcOfCircle CenterX=9.4 CenterY=1.5 CenterZ=0 NormalX=0 NormalY=0 NormalZ=1 AngleXU=0 Radius=1 StartAngle=3.27181 EndAngle=3.5951
    g89: LineSegment StartX=8.25982 StartY=1.5 StartZ=0 EndX=9.74018 EndY=1.5 EndZ=0
    g90: ArcOfCircle CenterX=10.2598 CenterY=1.35 CenterZ=0 NormalX=0 NormalY=0 NormalZ=1 AngleXU=0 Radius=0.149997 StartAngle=0.134719 EndAngle=1.57082
    g91: ArcOfCircle CenterX=11.7402 CenterY=1.35 CenterZ=0 NormalX=0 NormalY=0 NormalZ=1 AngleXU=0 Radius=0.15 StartAngle=1.5708 EndAngle=3.01411
    g92: ArcOfCircle CenterX=11 CenterY=1.30511 CenterZ=0 NormalX=0 NormalY=0 NormalZ=1 AngleXU=0 Radius=0.555048 StartAngle=3.59519 EndAngle=5.83002
    g93: ArcOfCircle CenterX=10.6 CenterY=1.5 CenterZ=0 NormalX=0 NormalY=0 NormalZ=1 AngleXU=0 Radius=1 StartAngle=5.82992 EndAngle=6.15188
    g94: ArcOfCircle CenterX=11.4 CenterY=1.5 CenterZ=0 NormalX=0 NormalY=0 NormalZ=1 AngleXU=0 Radius=1 StartAngle=3.27181 EndAngle=3.5951
    g95: LineSegment StartX=10.2598 StartY=1.5 StartZ=0 EndX=11.7402 EndY=1.5 EndZ=0
    g96: ArcOfCircle CenterX=12.2598 CenterY=1.35 CenterZ=0 NormalX=0 NormalY=0 NormalZ=1 AngleXU=0 Radius=0.149997 StartAngle=0.134719 EndAngle=1.57082
    g97: ArcOfCircle CenterX=13.7402 CenterY=1.35 CenterZ=0 NormalX=0 NormalY=0 NormalZ=1 AngleXU=0 Radius=0.15 StartAngle=1.5708 EndAngle=3.01411
    g98: ArcOfCircle CenterX=13 CenterY=1.30511 CenterZ=0 NormalX=0 NormalY=0 NormalZ=1 AngleXU=0 Radius=0.555048 StartAngle=3.59519 EndAngle=5.83002
    g99: ArcOfCircle CenterX=12.6 CenterY=1.5 CenterZ=0 NormalX=0 NormalY=0 NormalZ=1 AngleXU=0 Radius=1 StartAngle=5.82992 EndAngle=6.15188
    g100: ArcOfCircle CenterX=13.4 CenterY=1.5 CenterZ=0 NormalX=0 NormalY=0 NormalZ=1 AngleXU=0 Radius=1 StartAngle=3.27181 EndAngle=3.5951
    g101: LineSegment StartX=12.2598 StartY=1.5 StartZ=0 EndX=13.7402 EndY=1.5 EndZ=0
    g102: ArcOfCircle CenterX=14.2598 CenterY=1.35 CenterZ=0 NormalX=0 NormalY=0 NormalZ=1 AngleXU=0 Radius=0.149997 StartAngle=0.134719 EndAngle=1.57082
    g103: ArcOfCircle CenterX=15.7402 CenterY=1.35 CenterZ=0 NormalX=0 NormalY=0 NormalZ=1 AngleXU=0 Radius=0.15 StartAngle=1.5708 EndAngle=3.01411
    g104: ArcOfCircle CenterX=15 CenterY=1.30511 CenterZ=0 NormalX=0 NormalY=0 NormalZ=1 AngleXU=0 Radius=0.555048 StartAngle=3.59519 EndAngle=5.83002
    g105: ArcOfCircle CenterX=14.6 CenterY=1.5 CenterZ=0 NormalX=0 NormalY=0 NormalZ=1 AngleXU=0 Radius=1 StartAngle=5.82992 EndAngle=6.15188
    g106: ArcOfCircle CenterX=15.4 CenterY=1.5 CenterZ=0 NormalX=0 NormalY=0 NormalZ=1 AngleXU=0 Radius=1 StartAngle=3.27181 EndAngle=3.5951
    g107: LineSegment StartX=14.2598 StartY=1.5 StartZ=0 EndX=15.7402 EndY=1.5 EndZ=0
    g108: ArcOfCircle CenterX=16.2598 CenterY=1.35 CenterZ=0 NormalX=0 NormalY=0 NormalZ=1 AngleXU=0 Radius=0.149997 StartAngle=0.134719 EndAngle=1.57082
    g109: ArcOfCircle CenterX=17.7402 CenterY=1.35 CenterZ=0 NormalX=0 NormalY=0 NormalZ=1 AngleXU=0 Radius=0.15 StartAngle=1.5708 EndAngle=3.01411
    g110: ArcOfCircle CenterX=17 CenterY=1.30511 CenterZ=0 NormalX=0 NormalY=0 NormalZ=1 AngleXU=0 Radius=0.555048 StartAngle=3.59519 EndAngle=5.83002
    g111: ArcOfCircle CenterX=16.6 CenterY=1.5 CenterZ=0 NormalX=0 NormalY=0 NormalZ=1 AngleXU=0 Radius=1 StartAngle=5.82992 EndAngle=6.15188
    g112: ArcOfCircle CenterX=17.4 CenterY=1.5 CenterZ=0 NormalX=0 NormalY=0 NormalZ=1 AngleXU=0 Radius=1 StartAngle=3.27181 EndAngle=3.5951
    g113: LineSegment StartX=16.2598 StartY=1.5 StartZ=0 EndX=17.7402 EndY=1.5 EndZ=0
    g114: ArcOfCircle CenterX=18.2598 CenterY=1.35 CenterZ=0 NormalX=0 NormalY=0 NormalZ=1 AngleXU=0 Radius=0.149997 StartAngle=0.134719 EndAngle=1.57082
    g115: ArcOfCircle CenterX=19.7402 CenterY=1.35 CenterZ=0 NormalX=0 NormalY=0 NormalZ=1 AngleXU=0 Radius=0.15 StartAngle=1.5708 EndAngle=3.01411
    g116: ArcOfCircle CenterX=19 CenterY=1.30511 CenterZ=0 NormalX=0 NormalY=0 NormalZ=1 AngleXU=0 Radius=0.555048 StartAngle=3.59519 EndAngle=5.83002
    g117: ArcOfCircle CenterX=18.6 CenterY=1.5 CenterZ=0 NormalX=0 NormalY=0 NormalZ=1 AngleXU=0 Radius=1 StartAngle=5.82992 EndAngle=6.15188
    g118: ArcOfCircle CenterX=19.4 CenterY=1.5 CenterZ=0 NormalX=0 NormalY=0 NormalZ=1 AngleXU=0 Radius=1 StartAngle=3.27181 EndAngle=3.5951
    g119: LineSegment StartX=18.2598 StartY=1.5 StartZ=0 EndX=19.7402 EndY=1.5 EndZ=0
  constraints (140):
    c: Coincident(g0,g4)
    c: Coincident(g2,g4)
    c: Coincident(g2,g3)
    c: Coincident(g1,g3)
    c: Coincident(g5,g0)
    c: Tangent(g5,g1) = 1.5708
    c: Horizontal(g5)
    c: Coincident(g6,g10)
    c: Coincident(g12,g16)
    c: Coincident(g18,g22)
    c: Coincident(g24,g28)
    c: Coincident(g30,g34)
    c: Coincident(g36,g40)
    c: Coincident(g42,g46)
    c: Coincident(g48,g52)
    c: Coincident(g54,g58)
    c: Coincident(g60,g64)
    c: Coincident(g66,g70)
    c: Coincident(g72,g76)
    c: Coincident(g78,g82)
    c: Coincident(g84,g88)
    c: Coincident(g90,g94)
    c: Coincident(g96,g100)
    c: Coincident(g102,g106)
    c: Coincident(g108,g112)
    c: Coincident(g114,g118)
    c: Coincident(g8,g10)
    c: Coincident(g14,g16)
    c: Coincident(g20,g22)
    c: Coincident(g26,g28)
    c: Coincident(g32,g34)
    c: Coincident(g38,g40)
    c: Coincident(g44,g46)
    c: Coincident(g50,g52)
    c: Coincident(g56,g58)
    c: Coincident(g62,g64)
    c: Coincident(g68,g70)
    c: Coincident(g74,g76)
    c: Coincident(g80,g82)
    c: Coincident(g86,g88)
    c: Coincident(g92,g94)
    c: Coincident(g98,g100)
    c: Coincident(g104,g106)
    c: Coincident(g110,g112)
    c: Coincident(g116,g118)
    c: Coincident(g8,g9)
    c: Coincident(g14,g15)
    c: Coincident(g20,g21)
    c: Coincident(g26,g27)
    c: Coincident(g32,g33)
    c: Coincident(g38,g39)
    c: Coincident(g44,g45)
    c: Coincident(g50,g51)
    c: Coincident(g56,g57)
    c: Coincident(g62,g63)
    c: Coincident(g68,g69)
    c: Coincident(g74,g75)
    c: Coincident(g80,g81)
    c: Coincident(g86,g87)
    c: Coincident(g92,g93)
    c: Coincident(g98,g99)
    c: Coincident(g104,g105)
    c: Coincident(g110,g111)
    c: Coincident(g116,g117)
    c: Coincident(g7,g9)
    c: Coincident(g13,g15)
    c: Coincident(g19,g21)
    c: Coincident(g25,g27)
    c: Coincident(g31,g33)
    c: Coincident(g37,g39)
    c: Coincident(g43,g45)
    c: Coincident(g49,g51)
    c: Coincident(g55,g57)
    c: Coincident(g61,g63)
    c: Coincident(g67,g69)
    c: Coincident(g73,g75)
    c: Coincident(g79,g81)
    c: Coincident(g85,g87)
    c: Coincident(g91,g93)
    c: Coincident(g97,g99)
    c: Coincident(g103,g105)
    c: Coincident(g109,g111)
    c: Coincident(g115,g117)
    c: Coincident(g11,g6)
    c: Coincident(g17,g12)
    c: Coincident(g23,g18)
    c: Coincident(g29,g24)
    c: Coincident(g35,g30)
    c: Coincident(g41,g36)
    c: Coincident(g47,g42)
    c: Coincident(g53,g48)
    c: Coincident(g59,g54)
    c: Coincident(g65,g60)
    c: Coincident(g71,g66)
    c: Coincident(g77,g72)
    c: Coincident(g83,g78)
    c: Coincident(g89,g84)
    c: Coincident(g95,g90)
    c: Coincident(g101,g96)
    c: Coincident(g107,g102)
    c: Coincident(g113,g108)
    c: Coincident(g119,g114)
    c: Tangent(g11,g7) = 1.5708
    c: Tangent(g17,g13) = 1.5708
    c: Tangent(g23,g19) = 1.5708
    c: Tangent(g29,g25) = 1.5708
    c: Tangent(g35,g31) = 1.5708
    c: Tangent(g41,g37) = 1.5708
    c: Tangent(g47,g43) = 1.5708
    c: Tangent(g53,g49) = 1.5708
    c: Tangent(g59,g55) = 1.5708
    c: Tangent(g65,g61) = 1.5708
    c: Tangent(g71,g67) = 1.5708
    c: Tangent(g77,g73) = 1.5708
    c: Tangent(g83,g79) = 1.5708
    c: Tangent(g89,g85) = 1.5708
    c: Tangent(g95,g91) = 1.5708
    c: Tangent(g101,g97) = 1.5708
    c: Tangent(g107,g103) = 1.5708
    c: Tangent(g113,g109) = 1.5708
    c: Tangent(g119,g115) = 1.5708
    c: Horizontal(g11)
    c: Horizontal(g17)
    c: Horizontal(g23)
    c: Horizontal(g29)
    c: Horizontal(g35)
    c: Horizontal(g41)
    c: Horizontal(g47)
    c: Horizontal(g53)
    c: Horizontal(g59)
    c: Horizontal(g65)
    c: Horizontal(g71)
    c: Horizontal(g77)
    c: Horizontal(g83)
    c: Horizontal(g89)
    c: Horizontal(g95)
    c: Horizontal(g101)
    c: Horizontal(g107)
    c: Horizontal(g113)
    c: Horizontal(g119)
FEATURE [PartDesign::Pocket] Pocket017
  BaseFeature = -> Pad003
  Direction = (0,1,-2e-16)
  Length = 20
  Length2 = 5
  Profile = -> Sketch025
  ReferenceAxis = -> Sketch025 [N_Axis]
  Refine = true
  Suppressed = false
  Type = 0
FEATURE [Sketcher::SketchObject] Sketch027
  ArcFitTolerance = 1e-06
  AttachmentSupport = -> [Pocket017]
  FullyConstrained = false
  MakeInternals = false
  MapMode = 5
  Placement = pos=(0,0,0) rot=(1,0,0;3.14159rad)
  sketch-geometry (5):
    g0: GeomPoint [constr] X=0 Y=0 Z=0
    g1: Circle CenterX=-8 CenterY=-8 CenterZ=0 NormalX=0 NormalY=0 NormalZ=1 AngleXU=0 Radius=1.6
    g2: Circle CenterX=8 CenterY=-8 CenterZ=0 NormalX=0 NormalY=0 NormalZ=1 AngleXU=0 Radius=1.6
    g3: Circle CenterX=-8 CenterY=8 CenterZ=0 NormalX=0 NormalY=0 NormalZ=1 AngleXU=0 Radius=1.6
    g4: Circle CenterX=8 CenterY=8 CenterZ=0 NormalX=0 NormalY=0 NormalZ=1 AngleXU=0 Radius=1.6
FEATURE [PartDesign::Pocket] Pocket018
  BaseFeature = -> Pocket017
  Direction = (0,0,1)
  Length = 1.5
  Length2 = 5
  Profile = -> Sketch027
  ReferenceAxis = -> Sketch027 [N_Axis]
  Refine = true
  Suppressed = false
  Type = 0
FEATURE [PartDesign::Body] Body003
  AllowCompound = false
  Group = -> [Sketch024,Pad003,Sketch025,Pocket017,Sketch027,Pocket018]
  Origin = -> Origin010
  Tip = -> Pocket018
COMPONENT P4 — recipe-attached ("BaseCover", modeled in this document).
Construction recipe (the document's own serialized feature program — sketch geometry with constraints, then the solid features built on it; lengths are millimeters unless a unit is written):

FEATURE [Sketcher::SketchObject] Sketch026
  ArcFitTolerance = 1e-06
  AttachmentSupport = -> [XY_Plane011]
  FullyConstrained = false
  MakeInternals = false
  MapMode = 5
  sketch-geometry (9):
    g0: LineSegment StartX=-20 StartY=10 StartZ=0 EndX=-20 EndY=-10 EndZ=0
    g1: LineSegment StartX=-20 StartY=-10 StartZ=0 EndX=20 EndY=-10 EndZ=0
    g2: LineSegment StartX=20 StartY=-10 StartZ=0 EndX=20 EndY=10 EndZ=0
    g3: LineSegment StartX=20 StartY=10 StartZ=0 EndX=-20 EndY=10 EndZ=0
    g4: GeomPoint [constr] X=0 Y=0 Z=0
    g5: Circle CenterX=-8 CenterY=-8 CenterZ=0 NormalX=0 NormalY=0 NormalZ=1 AngleXU=0 Radius=1.6
    g6: Circle CenterX=8 CenterY=-8 CenterZ=0 NormalX=0 NormalY=0 NormalZ=1 AngleXU=0 Radius=1.6
    g7: Circle CenterX=-8 CenterY=8 CenterZ=0 NormalX=0 NormalY=0 NormalZ=1 AngleXU=0 Radius=1.6
    g8: Circle CenterX=8 CenterY=8 CenterZ=0 NormalX=0 NormalY=0 NormalZ=1 AngleXU=0 Radius=1.6
  constraints (8):
    c: Coincident(g0,g1)
    c: Coincident(g1,g2)
    c: Coincident(g2,g3)
    c: Coincident(g3,g0)
    c: Vertical(g0)
    c: Vertical(g2)
    c: Horizontal(g1)
    c: Horizontal(g3)
FEATURE [PartDesign::Pad] Pad004
  Direction = (0,0,1)
  Length = 1.5
  Length2 = 10
  Profile = -> Sketch026
  ReferenceAxis = -> Sketch026 [N_Axis]
  Refine = true
  Suppressed = false
  Type = 0
FEATURE [Sketcher::SketchObject] Sketch028
  ArcFitTolerance = 1e-06
  AttachmentSupport = -> [Pad004]
  FullyConstrained = false
  MakeInternals = false
  MapMode = 5
  Placement = pos=(-20,0,0) rot=(0.57735,-0.57735,-0.57735;2.0944rad)
  sketch-geometry (4):
    g0: LineSegment StartX=-3.1 StartY=1 StartZ=0 EndX=-3.1 EndY=0 EndZ=0
    g1: LineSegment StartX=-3.1 StartY=0 StartZ=0 EndX=3.1 EndY=0 EndZ=0
    g2: LineSegment StartX=3.1 StartY=0 StartZ=0 EndX=3.1 EndY=1 EndZ=0
    g3: LineSegment StartX=3.1 StartY=1 StartZ=0 EndX=-3.1 EndY=1 EndZ=0
  constraints (8):
    c: Coincident(g0,g1)
    c: Coincident(g1,g2)
    c: Coincident(g2,g3)
    c: Coincident(g3,g0)
    c: Vertical(g0)
    c: Vertical(g2)
    c: Horizontal(g1)
    c: Horizontal(g3)
FEATURE [PartDesign::Pocket] Pocket019
  BaseFeature = -> Pad004
  Direction = (1,0,0)
  Length = 40
  Length2 = 5
  Profile = -> Sketch028
  ReferenceAxis = -> Sketch028 [N_Axis]
  Refine = true
  Suppressed = false
  Type = 0
FEATURE [PartDesign::Body] Body004
  AllowCompound = false
  Group = -> [Sketch026,Pad004,Sketch028,Pocket019]
  Origin = -> Origin011
  Tip = -> Pocket019
PROVENANCE & LICENSES
A FreeCAD (.FCStd) document from a public repository crawl; recipes are the document's own serialized feature recipes (and, for linked parts, companion documents' recipes).
License: unknown-license-file.
